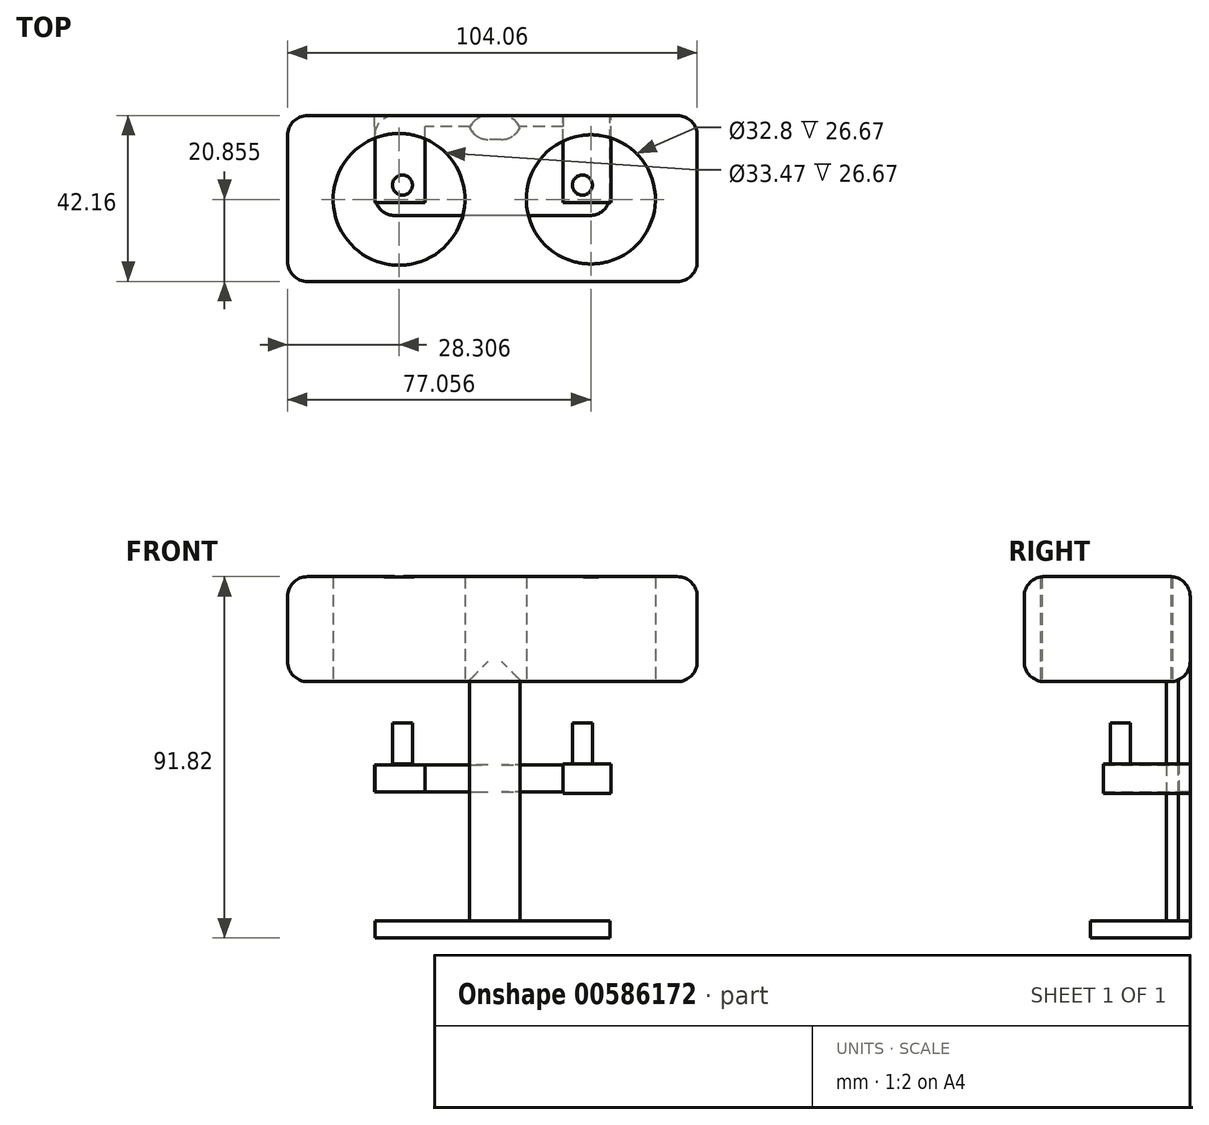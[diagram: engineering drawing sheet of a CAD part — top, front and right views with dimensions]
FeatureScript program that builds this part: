
annotation { "Feature Type Name" : "Feature", "Feature Type Description" : "" }
export const myFeature = defineFeature(function(context is Context, id is Id, definition is map)
    precondition{}
    {
        {
            var Q0;
            Q0=qCreatedBy(makeId("Front.planeOp"),FACE);
            var sketch = newSketch(context, id + "F0", { "sketchPlane" : qUnion([Q0])});
            skLineSegment(sketch, "E0.bottom", {"start": v(52.03, 13.34) * mm, "end": v(-52.03, 13.34) * mm});
            skLineSegment(sketch, "E0.top", {"start": v(52.03, -13.34) * mm, "end": v(-52.03, -13.34) * mm});
            skLineSegment(sketch, "E0.left", {"start": v(52.03, 13.34) * mm, "end": v(52.03, -13.34) * mm});
            skLineSegment(sketch, "E0.right", {"start": v(-52.03, 13.34) * mm, "end": v(-52.03, -13.34) * mm});
            skPoint(sketch, "E0.middle", {"position": v(0, 0) * mm});
            skSolve(sketch);
        }
        {
            var Q0;
            Q0=makeQuery(id+"F0.imprint","IMPRINT",FACE,{"disambiguationData":[TD([[makeQuery(id+"F0.imprint","IMPRINT",EDGE,{"derivedFrom":sQuery(id+"F0.wireOp",EDGE,"E0.bottom")}),1.0]])]});
            extrude(context, id + "F1", {"entities" : qUnion([Q0]), "depth" : 42.16 * mm, "offsetDistance" : 25.4 * mm});
        }
        {
            var Q0;
            Q0=makeQuery(id+"F1.opExtrude","CAP_EDGE",EDGE,{"disambiguationData":[OSD([sQuery(id+"F0.wireOp",EDGE,"E0.right")])],"isStart":false});
            fillet(context, id + "F2", {"entities" : qUnion([Q0]), "radius" : 5.08 * mm, "tangentPropagation" : true, "allowEdgeOverflow" : false});
        }
        {
            var Q0;
            Q0=makeQuery(id+"F1.opExtrude","CAP_EDGE",EDGE,{"disambiguationData":[OSD([sQuery(id+"F0.wireOp",EDGE,"E0.right")])],"isStart":true});
            fillet(context, id + "F3", {"entities" : qUnion([Q0]), "radius" : 5.08 * mm, "tangentPropagation" : true, "allowEdgeOverflow" : false});
        }
        {
            var Q0;
            Q0=makeQuery(id+"F1.opExtrude","CAP_EDGE",EDGE,{"disambiguationData":[OSD([sQuery(id+"F0.wireOp",EDGE,"E0.left")])],"isStart":false});
            fillet(context, id + "F4", {"entities" : qUnion([Q0]), "radius" : 5.08 * mm, "tangentPropagation" : true, "allowEdgeOverflow" : false});
        }
        {
            var Q0;
            Q0=makeQuery(id+"F1.opExtrude","CAP_EDGE",EDGE,{"disambiguationData":[OSD([sQuery(id+"F0.wireOp",EDGE,"E0.left")])],"isStart":true});
            fillet(context, id + "F5", {"entities" : qUnion([Q0]), "radius" : 5.08 * mm, "tangentPropagation" : true, "allowEdgeOverflow" : false});
        }
        {
            var Q0;
            Q0=qCreatedBy(makeId("Front.planeOp"),FACE);
            var sketch = newSketch(context, id + "F6", { "sketchPlane" : qUnion([Q0])});
            skLineSegment(sketch, "E1.bottom", {"start": v(7.4, -13.34) * mm, "end": v(-6.19, -13.34) * mm});
            skLineSegment(sketch, "E1.top", {"start": v(7.4, -76.09) * mm, "end": v(-6.19, -76.09) * mm});
            skLineSegment(sketch, "E1.left", {"start": v(7.4, -13.34) * mm, "end": v(7.4, -76.09) * mm});
            skLineSegment(sketch, "E1.right", {"start": v(-6.19, -13.34) * mm, "end": v(-6.19, -76.09) * mm});
            skSolve(sketch);
        }
        {
            var Q0;
            Q0 = qSketchRegion(id + "F6", true);
            extrude(context, id + "F7", {"entities" : qUnion([Q0]), "operationType" : NewBodyOperationType.ADD, "depth" : 6.1 * mm, "offsetDistance" : 25.4 * mm});
        }
        {
            var Q0;
            Q0=qCreatedBy(makeId("Front.planeOp"),FACE);
            var sketch = newSketch(context, id + "F8", { "sketchPlane" : qUnion([Q0])});
            skLineSegment(sketch, "E2.bottom", {"start": v(29.88, -78.48) * mm, "end": v(-29.88, -78.48) * mm});
            skLineSegment(sketch, "E2.top", {"start": v(29.88, -74.12) * mm, "end": v(-29.88, -74.12) * mm});
            skLineSegment(sketch, "E2.left", {"start": v(29.88, -78.48) * mm, "end": v(29.88, -74.12) * mm});
            skLineSegment(sketch, "E2.right", {"start": v(-29.88, -78.48) * mm, "end": v(-29.88, -74.12) * mm});
            skPoint(sketch, "E2.middle", {"position": v(0, -76.3) * mm});
            skSolve(sketch);
        }
        {
            var Q0;
            Q0 = qSketchRegion(id + "F8", true);
            extrude(context, id + "F9", {"entities" : qUnion([Q0]), "operationType" : NewBodyOperationType.ADD, "depth" : 25.4 * mm, "offsetDistance" : 25.4 * mm});
        }
        {
            var Q0;
            Q0=makeQuery(id+"F9.opExtrude","CAP_EDGE",EDGE,{"disambiguationData":[OSD([sQuery(id+"F8.wireOp",EDGE,"E2.right")])],"isStart":false});
            fillet(context, id + "F10", {"entities" : qUnion([Q0]), "radius" : 5.08 * mm, "tangentPropagation" : true, "allowEdgeOverflow" : false});
        }
        {
            var Q0;
            Q0=makeQuery(id+"F9.opExtrude","CAP_EDGE",EDGE,{"disambiguationData":[OSD([sQuery(id+"F8.wireOp",EDGE,"E2.right")])],"isStart":true});
            fillet(context, id + "F11", {"entities" : qUnion([Q0]), "radius" : 5.08 * mm, "tangentPropagation" : true, "allowEdgeOverflow" : false});
        }
        {
            var Q0;
            Q0=makeQuery(id+"F9.opExtrude","CAP_EDGE",EDGE,{"disambiguationData":[OSD([sQuery(id+"F8.wireOp",EDGE,"E2.left")])],"isStart":false});
            fillet(context, id + "F12", {"entities" : qUnion([Q0]), "radius" : 5.08 * mm, "tangentPropagation" : true, "allowEdgeOverflow" : false});
        }
        {
            var Q0;
            Q0=makeQuery(id+"F7.opExtrude","CAP_EDGE",EDGE,{"disambiguationData":[OSD([sQuery(id+"F6.wireOp",EDGE,"E1.right")])],"isStart":true});
            var Q1;
            Q1=makeQuery(id+"F7.opExtrude","CAP_EDGE",EDGE,{"disambiguationData":[OSD([sQuery(id+"F6.wireOp",EDGE,"E1.left")])],"isStart":true});
            var Q2;
            Q2=makeQuery(id+"F7.opExtrude","CAP_EDGE",EDGE,{"disambiguationData":[OSD([sQuery(id+"F6.wireOp",EDGE,"E1.left")])],"isStart":false});
            var Q3;
            Q3=makeQuery(id+"F7.opExtrude","CAP_EDGE",EDGE,{"disambiguationData":[OSD([sQuery(id+"F6.wireOp",EDGE,"E1.right")])],"isStart":false});
            fillet(context, id + "F13", {"entities" : qUnion([Q0, Q1, Q2, Q3]), "radius" : 5.08 * mm, "tangentPropagation" : true, "allowEdgeOverflow" : false});
        }
        {
            var Q0;
            Q0=qCreatedBy(makeId("Front.planeOp"),FACE);
            var sketch = newSketch(context, id + "F14", { "sketchPlane" : qUnion([Q0])});
            skLineSegment(sketch, "E3.bottom", {"start": v(29.97, -34.48) * mm, "end": v(-29.97, -34.48) * mm});
            skLineSegment(sketch, "E3.top", {"start": v(29.97, -41.39) * mm, "end": v(-29.97, -41.39) * mm});
            skLineSegment(sketch, "E3.left", {"start": v(29.97, -34.48) * mm, "end": v(29.97, -41.39) * mm});
            skLineSegment(sketch, "E3.right", {"start": v(-29.97, -34.48) * mm, "end": v(-29.97, -41.39) * mm});
            skPoint(sketch, "E3.middle", {"position": v(0, -37.93) * mm});
            skSolve(sketch);
        }
        {
            var Q0;
            Q0 = qSketchRegion(id + "F14", true);
            extrude(context, id + "F15", {"entities" : qUnion([Q0]), "operationType" : NewBodyOperationType.ADD, "depth" : 2.8 * mm, "offsetDistance" : 25.4 * mm});
        }
        {
            var Q0;
            Q0=qCreatedBy(makeId("Front.planeOp"),FACE);
            var sketch = newSketch(context, id + "F16", { "sketchPlane" : qUnion([Q0])});
            skLineSegment(sketch, "E4.bottom", {"start": v(-29.81, -34.49) * mm, "end": v(-17.07, -34.49) * mm});
            skLineSegment(sketch, "E4.top", {"start": v(-29.81, -41.39) * mm, "end": v(-17.07, -41.39) * mm});
            skLineSegment(sketch, "E4.left", {"start": v(-29.81, -34.49) * mm, "end": v(-29.81, -41.39) * mm});
            skLineSegment(sketch, "E4.right", {"start": v(-17.07, -34.49) * mm, "end": v(-17.07, -41.39) * mm});
            skLineSegment(sketch, "E5.bottom", {"start": v(17.96, -34.3) * mm, "end": v(30.16, -34.3) * mm});
            skLineSegment(sketch, "E5.top", {"start": v(17.96, -41.74) * mm, "end": v(30.16, -41.74) * mm});
            skLineSegment(sketch, "E5.left", {"start": v(17.96, -34.3) * mm, "end": v(17.96, -41.74) * mm});
            skLineSegment(sketch, "E5.right", {"start": v(30.16, -34.3) * mm, "end": v(30.16, -41.74) * mm});
            skSolve(sketch);
        }
        {
            var Q0;
            Q0 = qSketchRegion(id + "F16", true);
            extrude(context, id + "F17", {"entities" : qUnion([Q0]), "operationType" : NewBodyOperationType.ADD, "depth" : 22.1 * mm, "offsetDistance" : 25.4 * mm});
        }
        {
            var Q0;
            Q0=qCreatedBy(makeId("Top.planeOp"),FACE);
            var sketch = newSketch(context, id + "F18", { "sketchPlane" : qUnion([Q0])});
            skCircle(sketch, "E6", {"center": v(-23.72, -21.3) * mm, "radius": 16.74 * mm});
            skCircle(sketch, "E7", {"center": v(25.03, -21.3) * mm, "radius": 16.4 * mm});
            skSolve(sketch);
        }
        {
            var Q0;
            Q0=makeQuery(id+"F1.opExtrude","SWEPT_EDGE",EDGE,{"disambiguationData":[OSD([sQuery(id+"F0.wireOp",EDGE,"E0.bottom"),sQuery(id+"F0.wireOp",EDGE,"E0.right")])]});
            fillet(context, id + "F19", {"entities" : qUnion([Q0]), "radius" : 5.08 * mm, "tangentPropagation" : true, "allowEdgeOverflow" : false});
        }
        {
            var Q0;
            Q0=makeQuery(id+"F1.opExtrude","SWEPT_EDGE",EDGE,{"disambiguationData":[OSD([sQuery(id+"F0.wireOp",EDGE,"E0.top"),sQuery(id+"F0.wireOp",EDGE,"E0.right")])]});
            fillet(context, id + "F20", {"entities" : qUnion([Q0]), "radius" : 5.08 * mm, "tangentPropagation" : true, "allowEdgeOverflow" : false});
        }
        {
            var Q0;
            Q0=makeQuery(id+"F17.opExtrude","SWEPT_FACE",FACE,{"disambiguationData":[OSD([sQuery(id+"F16.wireOp",EDGE,"E5.bottom")])]});
            var sketch = newSketch(context, id + "F21", { "sketchPlane" : qUnion([Q0])});
            skCircle(sketch, "E8", {"center": v(22.85, -17.68) * mm, "radius": 2.54 * mm});
            skLineSegment(sketch, "E9", {"start": v(0, 3.69) * mm, "end": v(0, -49.53) * mm, "construction": true});
            skCircle(sketch, "E10.MirrorC", {"center": v(-22.85, -17.68) * mm, "radius": 2.54 * mm});
            skSolve(sketch);
        }
        {
            var Q0;
            Q0 = qSketchRegion(id + "F21", true);
            extrude(context, id + "F22", {"entities" : qUnion([Q0]), "operationType" : NewBodyOperationType.ADD, "depth" : 13.63 * mm, "offsetDistance" : 25.4 * mm});
        }
        {
            var Q0;
            Q0 = qSketchRegion(id + "F18", true);
            extrude(context, id + "F23", {"entities" : qUnion([Q0]), "operationType" : NewBodyOperationType.REMOVE, "endBound" : BoundingType.SYMMETRIC, "depth" : 47.75 * mm, "offsetDistance" : 25.4 * mm});
        }
    });
